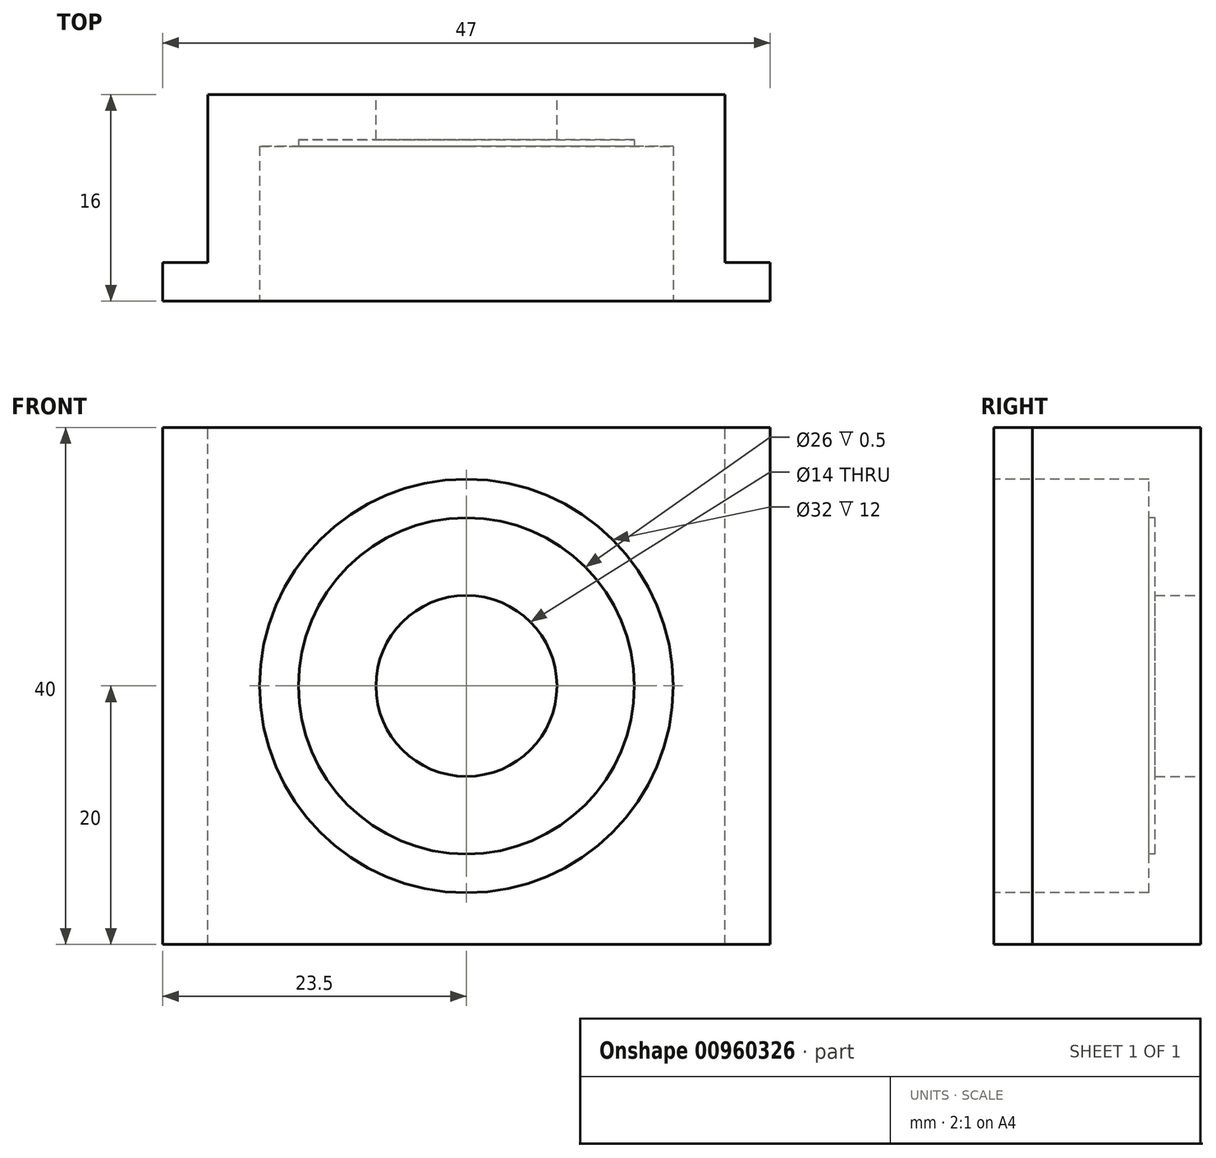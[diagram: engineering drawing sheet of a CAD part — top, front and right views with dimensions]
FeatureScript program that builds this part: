
annotation { "Feature Type Name" : "Feature", "Feature Type Description" : "" }
export const myFeature = defineFeature(function(context is Context, id is Id, definition is map)
    precondition{}
    {
        {
            var Q0;
            Q0=qCreatedBy(makeId("Front.planeOp"),FACE);
            var sketch = newSketch(context, id + "F0", { "sketchPlane" : qUnion([Q0])});
            skLineSegment(sketch, "E0.bottom", {"start": v(23.5, 20) * mm, "end": v(-23.5, 20) * mm});
            skLineSegment(sketch, "E0.top", {"start": v(23.5, -20) * mm, "end": v(-23.5, -20) * mm});
            skLineSegment(sketch, "E0.left", {"start": v(23.5, 20) * mm, "end": v(23.5, -20) * mm});
            skLineSegment(sketch, "E0.right", {"start": v(-23.5, 20) * mm, "end": v(-23.5, -20) * mm});
            skPoint(sketch, "E0.middle", {"position": v(0, 0) * mm});
            skCircle(sketch, "E1", {"center": v(0, 0) * mm, "radius": 7 * mm});
            skSolve(sketch);
        }
        {
            var Q0;
            Q0=makeQuery(id+"F0.imprint","IMPRINT",FACE,{"disambiguationData":[TD([[makeQuery(id+"F0.imprint","IMPRINT",EDGE,{"derivedFrom":sQuery(id+"F0.wireOp",EDGE,"E0.bottom")}),1.0]])]});
            extrude(context, id + "F1", {"entities" : qUnion([Q0]), "depth" : 16 * mm, "offsetDistance" : 25 * mm});
        }
        {
            var Q0;
            Q0=makeQuery(id+"F1.opExtrude","SWEPT_FACE",FACE,{"disambiguationData":[OSD([sQuery(id+"F0.wireOp",EDGE,"E0.bottom")])]});
            var sketch = newSketch(context, id + "F2", { "sketchPlane" : qUnion([Q0])});
            skLineSegment(sketch, "E2.bottom", {"start": v(-23.5, 0) * mm, "end": v(-20, 0) * mm});
            skLineSegment(sketch, "E2.top", {"start": v(-23.5, -13) * mm, "end": v(-20, -13) * mm});
            skLineSegment(sketch, "E2.left", {"start": v(-23.5, 0) * mm, "end": v(-23.5, -13) * mm});
            skLineSegment(sketch, "E2.right", {"start": v(-20, 0) * mm, "end": v(-20, -13) * mm});
            skLineSegment(sketch, "E3.MirrorCS", {"start": v(20, 0) * mm, "end": v(20, -13) * mm});
            skLineSegment(sketch, "E4.MirrorCS", {"start": v(23.5, -13) * mm, "end": v(20, -13) * mm});
            skSolve(sketch);
        }
        {
            var Q0;
            Q0=makeQuery(id+"F2.imprint","IMPRINT",FACE,{"disambiguationData":[TD([[makeQuery(id+"F2.imprint","IMPRINT",EDGE,{"derivedFrom":sQuery(id+"F2.wireOp",EDGE,"E2.bottom")}),1.0]])]});
            var Q1;
            {var subQ0=sQuery(id+"F2.wireOp",EDGE,"E3.MirrorCS");Q1=makeQuery(id+"F2.imprint","IMPRINT",FACE,{"disambiguationData":[TD([[makeQuery(id+"F2.imprint","IMPRINT",EDGE,{"derivedFrom":subQ0}),1.0]])]});}
            extrude(context, id + "F3", {"entities" : qUnion([Q0, Q1]), "operationType" : NewBodyOperationType.REMOVE, "endBound" : BoundingType.THROUGH_ALL, "oppositeDirection" : true, "depth" : 25 * mm, "offsetDistance" : 25 * mm});
        }
        {
            var Q0;
            Q0=makeQuery(id+"F1.opExtrude","CAP_FACE",FACE,{"disambiguationData":[OSD([sQuery(id+"F0.wireOp",EDGE,"E0.bottom"),sQuery(id+"F0.wireOp",EDGE,"E0.top"),sQuery(id+"F0.wireOp",EDGE,"E0.left"),sQuery(id+"F0.wireOp",EDGE,"E0.right"),sQuery(id+"F0.wireOp",EDGE,"E1")])],"isStart":false});
            var sketch = newSketch(context, id + "F4", { "sketchPlane" : qUnion([Q0])});
            skCircle(sketch, "E5", {"center": v(0, 0) * mm, "radius": 13 * mm});
            skCircle(sketch, "E6", {"center": v(0, 0) * mm, "radius": 16 * mm});
            skSolve(sketch);
        }
        {
            var Q0;
            Q0=makeQuery(id+"F4.imprint","IMPRINT",FACE,{"disambiguationData":[TD([[makeQuery(id+"F4.imprint","IMPRINT",EDGE,{"derivedFrom":sQuery(id+"F4.wireOp",EDGE,"E5")}),1.0]])]});
            extrude(context, id + "F5", {"entities" : qUnion([Q0]), "operationType" : NewBodyOperationType.REMOVE, "oppositeDirection" : true, "depth" : 12.5 * mm, "offsetDistance" : 25 * mm});
        }
        {
            var Q0;
            Q0=makeQuery(id+"F1.opExtrude","CAP_FACE",FACE,{"disambiguationData":[OSD([sQuery(id+"F0.wireOp",EDGE,"E0.bottom"),sQuery(id+"F0.wireOp",EDGE,"E0.top"),sQuery(id+"F0.wireOp",EDGE,"E0.left"),sQuery(id+"F0.wireOp",EDGE,"E0.right"),sQuery(id+"F0.wireOp",EDGE,"E1")])],"isStart":false});
            var sketch = newSketch(context, id + "F6", { "sketchPlane" : qUnion([Q0])});
            skCircle(sketch, "E7", {"center": v(0, 0) * mm, "radius": 16 * mm});
            skSolve(sketch);
        }
        {
            var Q0;
            Q0=makeQuery(id+"F6.imprint","IMPRINT",FACE,{"disambiguationData":[TD([[makeQuery(id+"F6.imprint","IMPRINT",EDGE,{"derivedFrom":sQuery(id+"F6.wireOp",EDGE,"E7")}),1.0]])]});
            extrude(context, id + "F7", {"entities" : qUnion([Q0]), "operationType" : NewBodyOperationType.REMOVE, "oppositeDirection" : true, "depth" : 12 * mm, "offsetDistance" : 25 * mm});
        }
    });
